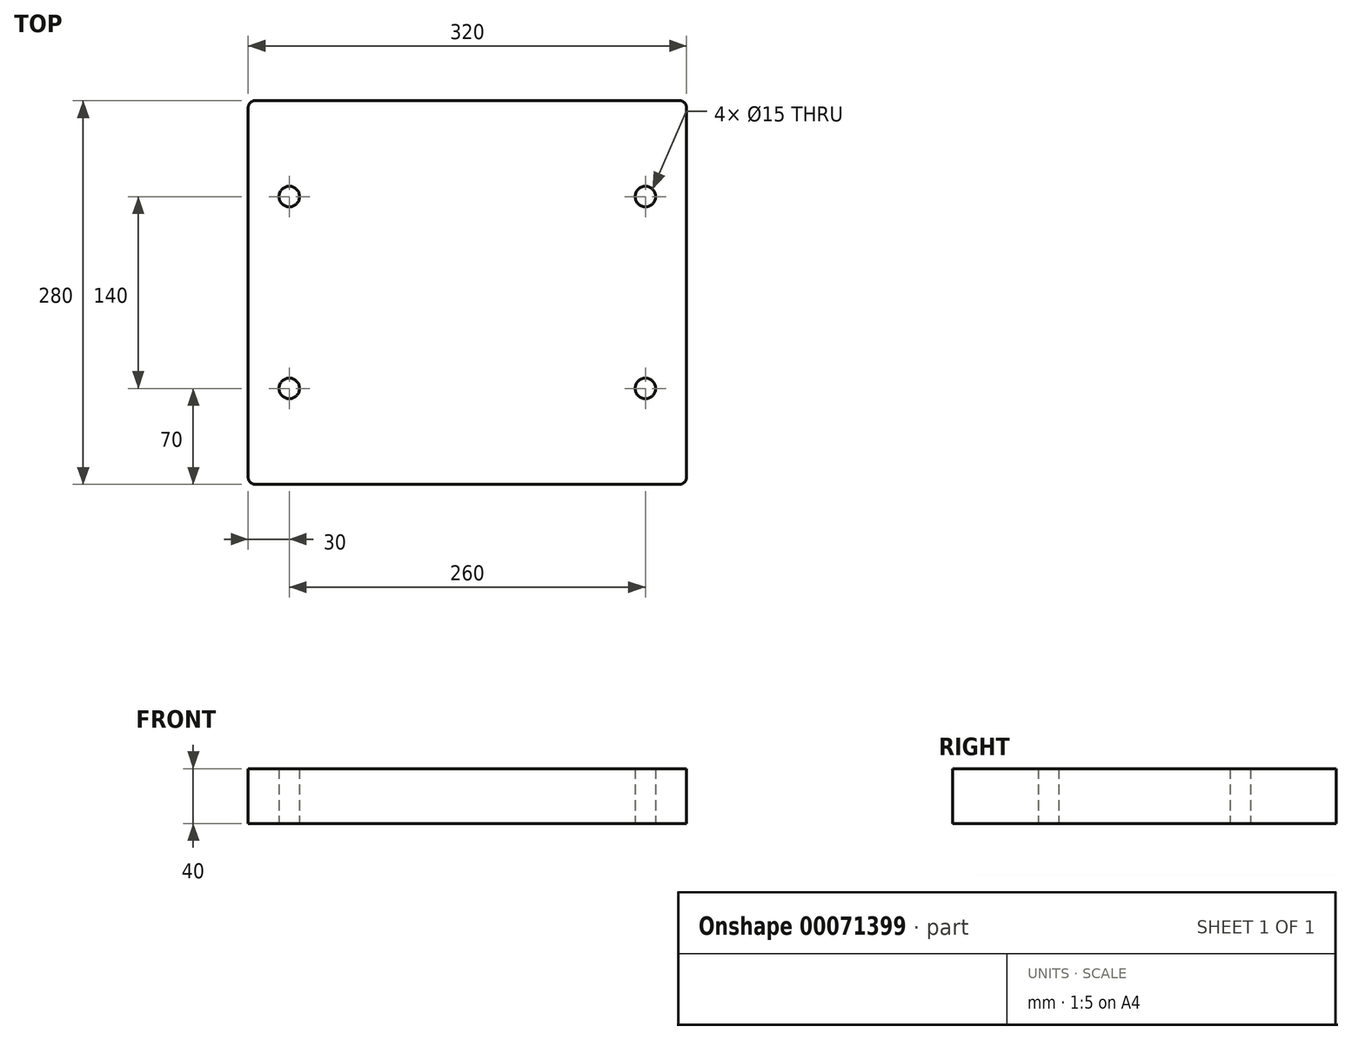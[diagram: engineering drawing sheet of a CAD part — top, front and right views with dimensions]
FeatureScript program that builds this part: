
annotation { "Feature Type Name" : "Feature", "Feature Type Description" : "" }
export const myFeature = defineFeature(function(context is Context, id is Id, definition is map)
    precondition{}
    {
        {
            var Q0;
            Q0=qCreatedBy(makeId("Top.planeOp"),FACE);
            var sketch = newSketch(context, id + "F0", { "sketchPlane" : qUnion([Q0])});
            skLineSegment(sketch, "E0.bottom", {"start": v(160, -140) * mm, "end": v(-160, -140) * mm});
            skLineSegment(sketch, "E0.top", {"start": v(160, 140) * mm, "end": v(-160, 140) * mm});
            skLineSegment(sketch, "E0.left", {"start": v(160, -140) * mm, "end": v(160, 140) * mm});
            skLineSegment(sketch, "E0.right", {"start": v(-160, -140) * mm, "end": v(-160, 140) * mm});
            skPoint(sketch, "E0.middle", {"position": v(0, 0) * mm});
            skCircle(sketch, "E1", {"center": v(130, -70) * mm, "radius": 7.5 * mm});
            skCircle(sketch, "E2", {"center": v(130, 70) * mm, "radius": 7.5 * mm});
            skCircle(sketch, "E3", {"center": v(-130, -70) * mm, "radius": 7.5 * mm});
            skCircle(sketch, "E4", {"center": v(-130, 70) * mm, "radius": 7.5 * mm});
            skSolve(sketch);
        }
        {
            var Q0;
            Q0=makeQuery(id+"F0.imprint","IMPRINT",FACE,{"disambiguationData":[TD([[makeQuery(id+"F0.imprint","IMPRINT",EDGE,{"derivedFrom":sQuery(id+"F0.wireOp",EDGE,"E0.bottom")}),-1.0]])]});
            extrude(context, id + "F1", {"entities" : qUnion([Q0]), "depth" : 40 * mm});
        }
        {
            var Q0;
            Q0=makeQuery(id+"F1.opExtrude","SWEPT_EDGE",EDGE,{"disambiguationData":[OSD([sQuery(id+"F0.wireOp",EDGE,"E0.bottom"),sQuery(id+"F0.wireOp",EDGE,"E0.right")])]});
            var Q1;
            Q1=makeQuery(id+"F1.opExtrude","SWEPT_EDGE",EDGE,{"disambiguationData":[OSD([sQuery(id+"F0.wireOp",EDGE,"E0.bottom"),sQuery(id+"F0.wireOp",EDGE,"E0.left")])]});
            var Q2;
            Q2=makeQuery(id+"F1.opExtrude","SWEPT_EDGE",EDGE,{"disambiguationData":[OSD([sQuery(id+"F0.wireOp",EDGE,"E0.top"),sQuery(id+"F0.wireOp",EDGE,"E0.left")])]});
            var Q3;
            Q3=makeQuery(id+"F1.opExtrude","SWEPT_EDGE",EDGE,{"disambiguationData":[OSD([sQuery(id+"F0.wireOp",EDGE,"E0.top"),sQuery(id+"F0.wireOp",EDGE,"E0.right")])]});
            fillet(context, id + "F2", {"entities" : qUnion([Q0, Q1, Q2, Q3]), "radius" : 5 * mm, "tangentPropagation" : true, "allowEdgeOverflow" : false});
        }
    });
